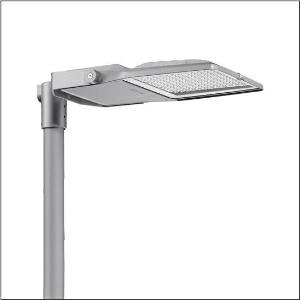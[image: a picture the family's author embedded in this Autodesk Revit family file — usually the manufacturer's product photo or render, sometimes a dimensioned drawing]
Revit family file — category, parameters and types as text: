
# Revit family: floodlight_fl_21_midi___pl43_5xa7785e2a3a_e2fe
name_source: partatom
category: Lighting Fixtures
units: mm (PartAtom-declared; Revit-internal decimal feet)

## family parameters
Cut with Voids When Loaded = No
Host = Face
Light Source = No
Part Type = Normal
Room Calculation Point = No
Round Connector Dimension = Use Diameter
Shared = No

## types (1)
- --- (1 x LED, 27640 lm, 212.4 W, 3000K)
    Apparent Load = 212 VA
    CIE Flux Codes = 27 78 99 100 100
    Color Rendering = 70
    Color Temperature = 3000K
    Default Elevation = 1800 mm
    Description = Floodlight FL 21 midi, floodlight, primary light control with lens, of PMMA, primary optical cover: protective disc, of toughened safety glass, transparent, light distribution: PL43, light emission: direct distribution, installation type: surface-mounted, LED, High Power LED, rated luminous flux: 27.640lm, luminous efficacy: 130lm/W, light colour: 730, colour temperature: 3000K, control gear: ECG Smart Interface, control: flexible luminous flux parameterisation, time-dependent luminous flux control, constant luminous flux control, overheat protection, presetting dimming logarithmic, with terminal, 6-pole, mains connection: 220..240V, AC, 50/60Hz, start of lifetime: 212W, end of service life: 231W, reduction: 95W, luminaire housing, of diecast aluminium, powder-coated, Siteco® metallic grey (DB 702S), sealing non-destructively replaceable, please order mast flange separately, mast bracket, of steel, galvanised, powder-coated, Siteco® metallic grey (DB 702S), Smart Interface above, protection rating (complete): IP66, insulation class (complete): insulation class II (safety insulation), certification: CE, protection symbol: D, impact resistance: IK08, permissible operating ambient temperature: -20..+40°C, permissible operating ambient temperature for outdoor applications: -40..+50°C, standard: DIN EN 12944, LABS conformity tested according to VDMA 24364:2018-05, packaging unit: 1 piece

Light Distribution: PL43
    Height = 76 mm
    Lamp = 1 x LED
    Lamp Light Flux = 27640 lm
    Lamp Power = 212.4 W
    Lamp count = 1
    Length = 657 mm
    Luminous efficacy = 130 lm/W
    Manufacturer = Siteco
    ModVariant = No
    Model = 5XA7785E2A3A
    Number of Poles = 1
    OnlyDefault = Yes
    Power Factor = 1
    Product Name = Floodlight FL 21 midi | PL43
    Product group = floodlight | pylon annexe
    ProductGroupID = 6200
    Protection Class = Protection class II
    Protection Degree = IP 66
    RLX_Detail_Level = 1
    RLX_Emergency_Light_Flux = 0 lm
    RLX_Emergency_Type = 0
    RLX_Emergency_Type_DB = No
    RlxData = <blob elided: 153285 chars, md5=76be70c4>
    Socket = socket
    Standby Power = 0 W
    System Light Flux = 27640 lm
    System Power = 212 W
    Type Comments = factory setting: luminous flux: 100 % | dim-lin: 254 | 710 mA
    Type Image = l_1007123.jpg
    URL = http://relux.com
    VarID = @adj_128511
    Voltage = 0 V
    Weight = 0.00 kg
    Width = 442 mm

## geometry (parser evidence)
native form markers: Blend x4, Sweep x14
no freeform markers — native parametric forms only
